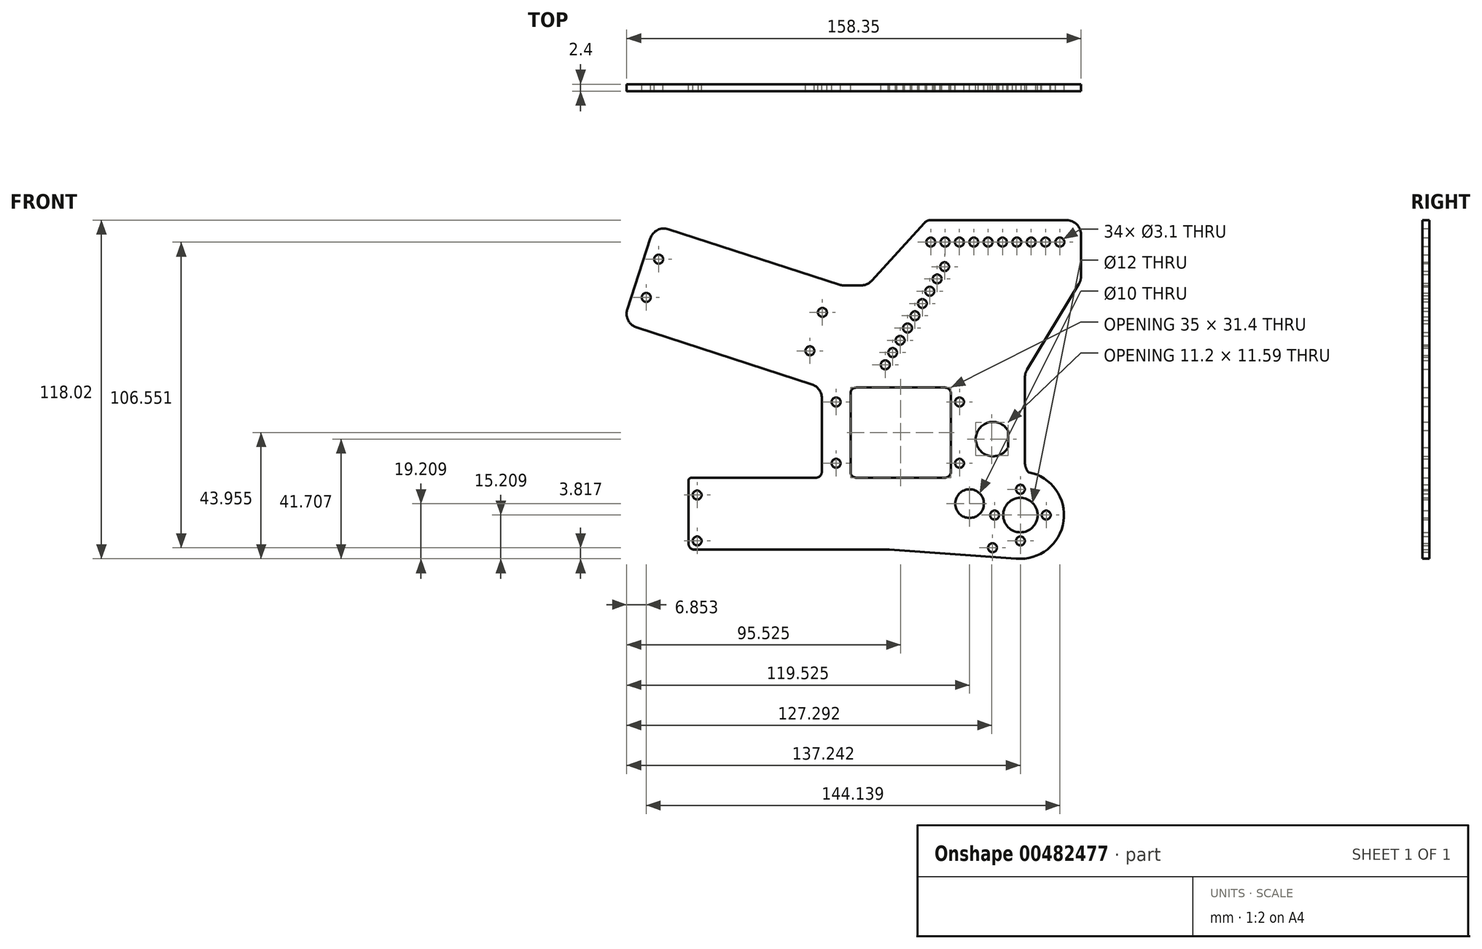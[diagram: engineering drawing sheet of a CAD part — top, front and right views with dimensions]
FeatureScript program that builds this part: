
annotation { "Feature Type Name" : "Feature", "Feature Type Description" : "" }
export const myFeature = defineFeature(function(context is Context, id is Id, definition is map)
    precondition{}
    {
        {
            var Q0;
            Q0=qCreatedBy(makeId("Front.planeOp"),FACE);
            var sketch = newSketch(context, id + "F0", { "sketchPlane" : qUnion([Q0])});
            skLineSegment(sketch, "E0.bottom", {"start": v(-102.71, -14.41) * mm, "end": v(-6.71, -14.41) * mm, "construction": true});
            skLineSegment(sketch, "E0.top", {"start": v(-102.71, -60.91) * mm, "end": v(-6.71, -60.91) * mm, "construction": true});
            skLineSegment(sketch, "E0.left", {"start": v(-102.71, -14.41) * mm, "end": v(-102.71, -60.91) * mm, "construction": true});
            skLineSegment(sketch, "E0.right", {"start": v(-6.71, -14.41) * mm, "end": v(-6.71, -60.91) * mm, "construction": true});
            skLineSegment(sketch, "E1", {"start": v(-107.21, -36.41) * mm, "end": v(-40.67, -36.41) * mm});
            skLineSegment(sketch, "E2", {"start": v(-131.69, 48.27) * mm, "end": v(-110.06, 41.24) * mm});
            skLineSegment(sketch, "E3", {"start": v(-110.06, 41.24) * mm, "end": v(-76.45, 30.32) * mm});
            skPoint(sketch, "E4", {"position": v(5, -24.41) * mm});
            skLineSegment(sketch, "E5", {"start": v(-132, 47.31) * mm, "end": v(-123.96, 72.04) * mm});
            skLineSegment(sketch, "E6", {"start": v(-52.21, -11.36) * mm, "end": v(-21.21, -11.36) * mm});
            skLineSegment(sketch, "E7", {"start": v(-19.21, -9.36) * mm, "end": v(-19.21, 18.03) * mm});
            skCircle(sketch, "E8", {"center": v(5, -24.41) * mm, "radius": 6 * mm});
            skLineSegment(sketch, "E9", {"start": v(-54.21, -9.36) * mm, "end": v(-54.21, 18.03) * mm});
            skLineSegment(sketch, "E10", {"start": v(7.33, 26.3) * mm, "end": v(23.46, 53) * mm});
            skLineSegment(sketch, "E11", {"start": v(0.65, 5.08) * mm, "end": v(0.65, -0.9) * mm});
            skArc(sketch, "E12", {"start": v(0.65, 5.08) * mm, "mid": v(-10.55, 2.09) * mm, "end": v(0.65, -0.9) * mm});
            skLineSegment(sketch, "E13", {"start": v(6.6, -6.23) * mm, "end": v(6.6, 23.71) * mm});
            skLineSegment(sketch, "E14.trimOffspring", {"start": v(7.44, -9) * mm, "end": v(7.68, -9.36) * mm});
            skLineSegment(sketch, "E15", {"start": v(23.46, 53) * mm, "end": v(25.4, 56.2) * mm});
            skLineSegment(sketch, "E16", {"start": v(21.11, 78.4) * mm, "end": v(-26.3, 78.4) * mm});
            skLineSegment(sketch, "E17", {"start": v(-69.22, -11.36) * mm, "end": v(-107.21, -11.36) * mm});
            skLineSegment(sketch, "E18", {"start": v(-128.79, 41.01) * mm, "end": v(-67.67, 21.16) * mm});
            skLineSegment(sketch, "E19", {"start": v(-64.21, 16.4) * mm, "end": v(-64.21, -9.36) * mm});
            skLineSegment(sketch, "E20", {"start": v(-69.22, -11.36) * mm, "end": v(-66.21, -11.36) * mm});
            skLineSegment(sketch, "E21", {"start": v(-52.21, 20.03) * mm, "end": v(-21.21, 20.03) * mm});
            skLineSegment(sketch, "E22", {"start": v(-69.03, 53.14) * mm, "end": v(-124.27, 71.1) * mm});
            skLineSegment(sketch, "E23", {"start": v(-117.66, 75.25) * mm, "end": v(-67.18, 58.85) * mm});
            skLineSegment(sketch, "E24", {"start": v(-67.18, 58.85) * mm, "end": v(-58.15, 55.92) * mm});
            skLineSegment(sketch, "E25", {"start": v(-56.6, 55.67) * mm, "end": v(-50.52, 55.67) * mm});
            skLineSegment(sketch, "E26", {"start": v(-46.82, 57.3) * mm, "end": v(-28.52, 77.42) * mm});
            skLineSegment(sketch, "E27", {"start": v(26.11, 58.78) * mm, "end": v(26.11, 73.4) * mm});
            skLineSegment(sketch, "E28", {"start": v(-16.25, 70.75) * mm, "end": v(-42.1, 27.95) * mm, "construction": true});
            skPoint(sketch, "E29", {"position": v(-125.39, 51.48) * mm});
            skPoint(sketch, "E30", {"position": v(-121.06, 64.8) * mm});
            skLineSegment(sketch, "E31", {"start": v(-69.03, 53.14) * mm, "end": v(-63.2, 51.25) * mm});
            skLineSegment(sketch, "E32", {"start": v(-70.64, 28.34) * mm, "end": v(-76.45, 30.32) * mm});
            skLineSegment(sketch, "E33", {"start": v(-63.2, 51.25) * mm, "end": v(-57.7, 49.46) * mm});
            skLineSegment(sketch, "E34", {"start": v(-57.7, 49.46) * mm, "end": v(-65.14, 26.55) * mm});
            skLineSegment(sketch, "E35", {"start": v(-70.64, 28.34) * mm, "end": v(-65.14, 26.55) * mm});
            skPoint(sketch, "E36", {"position": v(-64, 46.25) * mm});
            skPoint(sketch, "E37", {"position": v(-68.35, 32.85) * mm});
            skCircle(sketch, "E38", {"center": v(-12.71, -20.41) * mm, "radius": 5 * mm});
            skCircle(sketch, "E39", {"center": v(-21.42, 62.19) * mm, "radius": 1.55 * mm});
            skCircle(sketch, "E40", {"center": v(-24, 57.9) * mm, "radius": 1.55 * mm});
            skCircle(sketch, "E41", {"center": v(-26.6, 53.63) * mm, "radius": 1.55 * mm});
            skCircle(sketch, "E42", {"center": v(-29.18, 49.35) * mm, "radius": 1.55 * mm});
            skCircle(sketch, "E43", {"center": v(-31.76, 45.07) * mm, "radius": 1.55 * mm});
            skCircle(sketch, "E44", {"center": v(-34.35, 40.8) * mm, "radius": 1.55 * mm});
            skCircle(sketch, "E45", {"center": v(-36.93, 36.51) * mm, "radius": 1.55 * mm});
            skCircle(sketch, "E46", {"center": v(-39.52, 32.23) * mm, "radius": 1.55 * mm});
            skCircle(sketch, "E47", {"center": v(-42.1, 27.95) * mm, "radius": 1.55 * mm});
            skPoint(sketch, "E48", {"position": v(-90.98, 60.28) * mm});
            skPoint(sketch, "E49", {"position": v(-98.4, 37.45) * mm});
            skLineSegment(sketch, "E50", {"start": v(-90.98, 60.28) * mm, "end": v(-87.52, 70.94) * mm, "construction": true});
            skLineSegment(sketch, "E51", {"start": v(-87.52, 70.94) * mm, "end": v(-101.09, 29.18) * mm, "construction": true});
            skPoint(sketch, "E52.visualSharp", {"position": v(-19.21, 20.03) * mm});
            skArc(sketch, "E52.filletArc", {"start": v(-19.21, 18.03) * mm, "mid": v(-19.8, 19.45) * mm, "end": v(-21.21, 20.03) * mm});
            skPoint(sketch, "E53.visualSharp", {"position": v(-54.21, 20.03) * mm});
            skArc(sketch, "E53.filletArc", {"start": v(-52.21, 20.03) * mm, "mid": v(-53.63, 19.45) * mm, "end": v(-54.21, 18.03) * mm});
            skPoint(sketch, "E54.visualSharp", {"position": v(-19.21, -11.36) * mm});
            skArc(sketch, "E54.filletArc", {"start": v(-21.21, -11.36) * mm, "mid": v(-19.8, -10.78) * mm, "end": v(-19.21, -9.36) * mm});
            skPoint(sketch, "E55.visualSharp", {"position": v(-54.21, -11.36) * mm});
            skArc(sketch, "E55.filletArc", {"start": v(-54.21, -9.36) * mm, "mid": v(-53.63, -10.78) * mm, "end": v(-52.21, -11.36) * mm});
            skPoint(sketch, "E56.visualSharp", {"position": v(-109.21, -11.36) * mm});
            skArc(sketch, "E56.filletArc", {"start": v(-107.21, -11.36) * mm, "mid": v(-107.23, -11.36) * mm, "end": v(-107.24, -11.36) * mm});
            skPoint(sketch, "E57.visualSharp", {"position": v(-64.21, -11.36) * mm});
            skArc(sketch, "E57.filletArc", {"start": v(-66.21, -11.36) * mm, "mid": v(-64.8, -10.78) * mm, "end": v(-64.21, -9.36) * mm});
            skPoint(sketch, "E58.visualSharp", {"position": v(-64.21, 20.03) * mm});
            skArc(sketch, "E58.filletArc", {"start": v(-64.21, 16.4) * mm, "mid": v(-65.17, 19.34) * mm, "end": v(-67.67, 21.16) * mm});
            skPoint(sketch, "E59.visualSharp", {"position": v(-133.54, 42.56) * mm});
            skArc(sketch, "E59.filletArc", {"start": v(-132, 47.31) * mm, "mid": v(-131.7, 43.5) * mm, "end": v(-128.79, 41.01) * mm});
            skPoint(sketch, "E60.visualSharp", {"position": v(-122.42, 76.8) * mm});
            skArc(sketch, "E60.filletArc", {"start": v(-117.66, 75.25) * mm, "mid": v(-121.48, 74.95) * mm, "end": v(-123.96, 72.04) * mm});
            skPoint(sketch, "E61.visualSharp", {"position": v(26.11, 78.4) * mm});
            skArc(sketch, "E61.filletArc", {"start": v(26.11, 73.4) * mm, "mid": v(24.65, 76.93) * mm, "end": v(21.11, 78.4) * mm});
            skPoint(sketch, "E62.visualSharp", {"position": v(6.6, 25.1) * mm});
            skArc(sketch, "E62.filletArc", {"start": v(7.33, 26.3) * mm, "mid": v(6.79, 25.05) * mm, "end": v(6.6, 23.71) * mm});
            skPoint(sketch, "E63.visualSharp", {"position": v(6.6, -7.74) * mm});
            skArc(sketch, "E63.filletArc", {"start": v(6.6, -6.23) * mm, "mid": v(6.82, -7.68) * mm, "end": v(7.44, -9) * mm});
            skPoint(sketch, "E64.visualSharp", {"position": v(7.74, -9.45) * mm});
            skArc(sketch, "E64.filletArc", {"start": v(7.68, -9.36) * mm, "mid": v(7.75, -9.43) * mm, "end": v(7.85, -9.47) * mm});
            skPoint(sketch, "E65.visualSharp", {"position": v(-109.21, -36.41) * mm});
            skPoint(sketch, "E66.visualSharp", {"position": v(-27.63, 78.4) * mm});
            skArc(sketch, "E66.filletArc", {"start": v(-26.3, 78.4) * mm, "mid": v(-27.52, 78.14) * mm, "end": v(-28.52, 77.42) * mm});
            skPoint(sketch, "E67.visualSharp", {"position": v(-48.3, 55.67) * mm});
            skArc(sketch, "E67.filletArc", {"start": v(-50.52, 55.67) * mm, "mid": v(-48.5, 56.1) * mm, "end": v(-46.82, 57.3) * mm});
            skPoint(sketch, "E68.visualSharp", {"position": v(-57.4, 55.67) * mm});
            skArc(sketch, "E68.filletArc", {"start": v(-58.15, 55.92) * mm, "mid": v(-57.39, 55.73) * mm, "end": v(-56.6, 55.67) * mm});
            skPoint(sketch, "E69.visualSharp", {"position": v(26.11, 57.4) * mm});
            skArc(sketch, "E69.filletArc", {"start": v(25.4, 56.2) * mm, "mid": v(25.93, 57.44) * mm, "end": v(26.11, 58.78) * mm});
            skCircle(sketch, "E70", {"center": v(-107.65, -17.41) * mm, "radius": 1.55 * mm});
            skCircle(sketch, "E71", {"center": v(-107.65, -33.41) * mm, "radius": 1.55 * mm});
            skLineSegment(sketch, "E72", {"start": v(-66.21, -11.36) * mm, "end": v(-52.21, -11.36) * mm, "construction": true});
            skCircle(sketch, "E73", {"center": v(-59.21, -6.36) * mm, "radius": 1.55 * mm});
            skPoint(sketch, "E73.centerSnap0", {"position": v(-59.21, -11.36) * mm});
            skLineSegment(sketch, "E74", {"start": v(-52.21, 20.03) * mm, "end": v(-65.78, 20.03) * mm, "construction": true});
            skCircle(sketch, "E75", {"center": v(-59.21, 15.03) * mm, "radius": 1.55 * mm});
            skLineSegment(sketch, "E76", {"start": v(-59.21, 15.03) * mm, "end": v(-11.94, 15.03) * mm, "construction": true});
            skLineSegment(sketch, "E77", {"start": v(-59.21, -6.36) * mm, "end": v(-11.7, -6.36) * mm, "construction": true});
            skCircle(sketch, "E78", {"center": v(-16.21, 15.03) * mm, "radius": 1.55 * mm});
            skCircle(sketch, "E79", {"center": v(-16.21, -6.36) * mm, "radius": 1.55 * mm});
            skLineSegment(sketch, "E80", {"start": v(3.54, -39.55) * mm, "end": v(-40.67, -36.41) * mm});
            skCircle(sketch, "E81", {"center": v(-4.71, -35.8) * mm, "radius": 3 * mm, "construction": true});
            skArc(sketch, "E82.trimOffspring", {"start": v(3.54, -39.55) * mm, "mid": v(20.06, -26.57) * mm, "end": v(7.85, -9.47) * mm});
            skCircle(sketch, "E83", {"center": v(-4.71, -35.8) * mm, "radius": 1.55 * mm});
            skLineSegment(sketch, "E84.trimOffspring", {"start": v(-7.65, -36.41) * mm, "end": v(-6.71, -36.41) * mm});
            skLineSegment(sketch, "E85", {"start": v(-110.65, -12.38) * mm, "end": v(-110.65, -34.43) * mm});
            skLineSegment(sketch, "E86", {"start": v(-108.62, -36.43) * mm, "end": v(-107.21, -36.41) * mm});
            skLineSegment(sketch, "E87", {"start": v(-109.66, -11.38) * mm, "end": v(-107.21, -11.36) * mm});
            skPoint(sketch, "E88.visualSharp", {"position": v(-110.65, -11.39) * mm});
            skArc(sketch, "E88.filletArc", {"start": v(-109.66, -11.38) * mm, "mid": v(-110.36, -11.67) * mm, "end": v(-110.65, -12.38) * mm});
            skPoint(sketch, "E89.visualSharp", {"position": v(-110.65, -36.47) * mm});
            skArc(sketch, "E89.filletArc", {"start": v(-110.65, -34.43) * mm, "mid": v(-110.06, -35.86) * mm, "end": v(-108.62, -36.43) * mm});
            skCircle(sketch, "E90", {"center": v(-121.06, 64.8) * mm, "radius": 1.55 * mm});
            skCircle(sketch, "E91", {"center": v(-125.39, 51.48) * mm, "radius": 1.55 * mm});
            skCircle(sketch, "E92", {"center": v(-64, 46.25) * mm, "radius": 1.55 * mm});
            skCircle(sketch, "E93", {"center": v(-68.35, 32.85) * mm, "radius": 1.55 * mm});
            skArc(sketch, "E94", {"start": v(14, -24.41) * mm, "mid": v(11.9, -18.62) * mm, "end": v(6.55, -15.54) * mm, "construction": true});
            skCircle(sketch, "E95", {"center": v(-4, -24.41) * mm, "radius": 1.55 * mm});
            skCircle(sketch, "E96", {"center": v(5, -15.41) * mm, "radius": 1.55 * mm});
            skCircle(sketch, "E97", {"center": v(14, -24.41) * mm, "radius": 1.55 * mm});
            skCircle(sketch, "E98", {"center": v(5, -33.41) * mm, "radius": 1.55 * mm});
            skLineSegment(sketch, "E99", {"start": v(-16.25, 70.75) * mm, "end": v(21.56, 70.75) * mm, "construction": true});
            skCircle(sketch, "E100", {"center": v(-16.25, 70.75) * mm, "radius": 1.55 * mm});
            skLineSegment(sketch, "E101", {"start": v(-16.25, 70.75) * mm, "end": v(-29.03, 70.75) * mm, "construction": true});
            skCircle(sketch, "E102", {"center": v(-21.25, 70.75) * mm, "radius": 1.55 * mm});
            skCircle(sketch, "E103", {"center": v(-26.25, 70.75) * mm, "radius": 1.55 * mm});
            skCircle(sketch, "E104", {"center": v(-11.25, 70.75) * mm, "radius": 1.55 * mm});
            skCircle(sketch, "E105", {"center": v(-6.25, 70.75) * mm, "radius": 1.55 * mm});
            skLineSegment(sketch, "E106", {"start": v(-3.75, 74.91) * mm, "end": v(-3.75, 67.65) * mm, "construction": true});
            skCircle(sketch, "E107.MirrorC", {"center": v(-1.25, 70.75) * mm, "radius": 1.55 * mm});
            skCircle(sketch, "E108.MirrorC", {"center": v(3.75, 70.75) * mm, "radius": 1.55 * mm});
            skCircle(sketch, "E109.MirrorC", {"center": v(8.75, 70.75) * mm, "radius": 1.55 * mm});
            skCircle(sketch, "E110.MirrorC", {"center": v(13.75, 70.75) * mm, "radius": 1.55 * mm});
            skCircle(sketch, "E111.MirrorC", {"center": v(18.75, 70.75) * mm, "radius": 1.55 * mm});
            skLineSegment(sketch, "E112", {"start": v(-59.21, 1.1) * mm, "end": v(-59.21, -20.4) * mm, "construction": true});
            skLineSegment(sketch, "E113", {"start": v(-16.21, 4.66) * mm, "end": v(-16.21, -20.68) * mm, "construction": true});
            skPoint(sketch, "E114.end.orphan", {"position": v(-90.18, 62.75) * mm});
            skPoint(sketch, "E115.end.orphan", {"position": v(-109.2, 68.93) * mm});
            skPoint(sketch, "E115.start.orphan", {"position": v(-110, 66.46) * mm});
            skPoint(sketch, "E116.MirrorCS.start.orphan", {"position": v(-71.16, 56.57) * mm});
            skPoint(sketch, "E117.MirrorCS.start.orphan", {"position": v(-71.96, 54.1) * mm});
            skPoint(sketch, "E118.start.orphan", {"position": v(-117.42, 43.63) * mm});
            skPoint(sketch, "E119.end.orphan", {"position": v(-99.2, 34.98) * mm});
            skPoint(sketch, "E119.start.orphan", {"position": v(-118.22, 41.16) * mm});
            skPoint(sketch, "E120.MirrorCS.start.orphan", {"position": v(-80.18, 28.8) * mm});
            skPoint(sketch, "E121.MirrorCS.start.orphan", {"position": v(-79.38, 31.27) * mm});
            skSolve(sketch);
        }
        {
            var Q0;
            Q0 = qSketchRegion(id + "F0", true);
            extrude(context, id + "F1", {"entities" : qUnion([Q0]), "depth" : 2.4 * mm, "offsetDistance" : 25 * mm});
        }
    });
